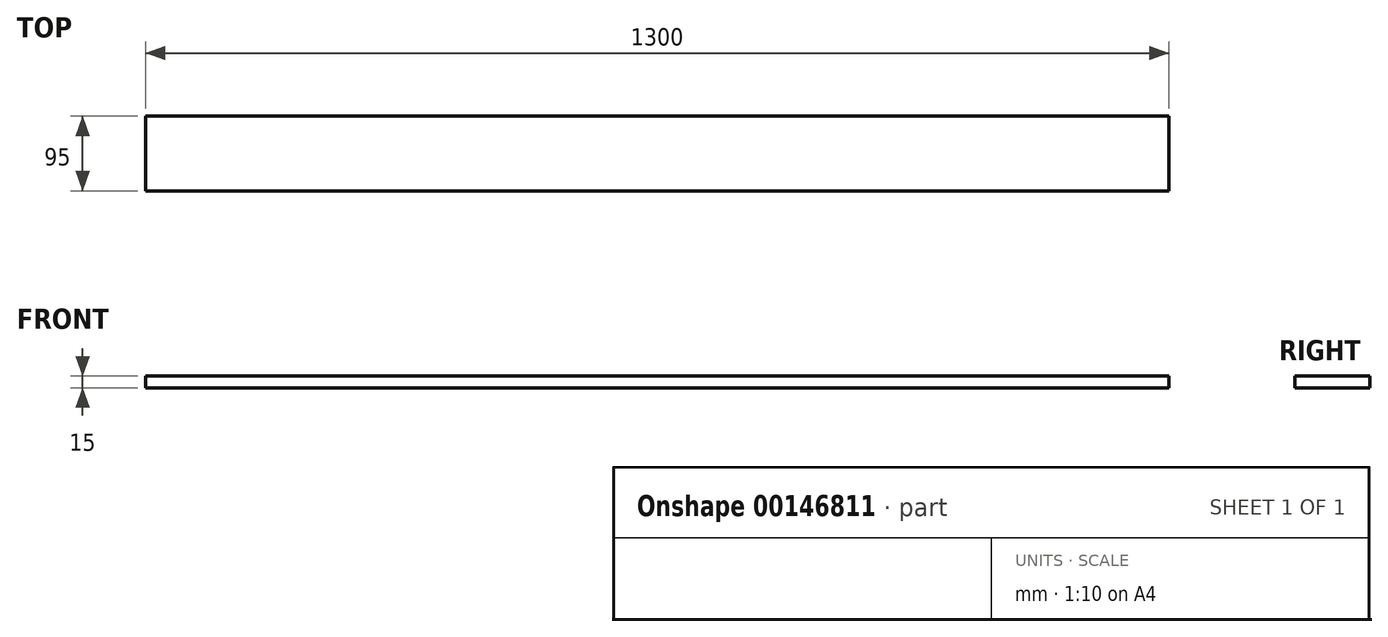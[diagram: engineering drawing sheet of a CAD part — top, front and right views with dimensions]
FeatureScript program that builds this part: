
annotation { "Feature Type Name" : "Feature", "Feature Type Description" : "" }
export const myFeature = defineFeature(function(context is Context, id is Id, definition is map)
    precondition{}
    {
        {
            var Q0;
            Q0=qCreatedBy(makeId("Top.planeOp"),FACE);
            var sketch = newSketch(context, id + "F0", { "sketchPlane" : qUnion([Q0])});
            skLineSegment(sketch, "E0.bottom", {"start": v(0, 0) * mm, "end": v(1300, 0) * mm});
            skLineSegment(sketch, "E0.top", {"start": v(0, 95) * mm, "end": v(1300, 95) * mm});
            skLineSegment(sketch, "E0.left", {"start": v(0, 0) * mm, "end": v(0, 95) * mm});
            skLineSegment(sketch, "E0.right", {"start": v(1300, 0) * mm, "end": v(1300, 95) * mm});
            skSolve(sketch);
        }
        {
            var Q0;
            Q0 = qSketchRegion(id + "F0", true);
            extrude(context, id + "F1", {"entities" : qUnion([Q0]), "depth" : 15 * mm});
        }
    });
